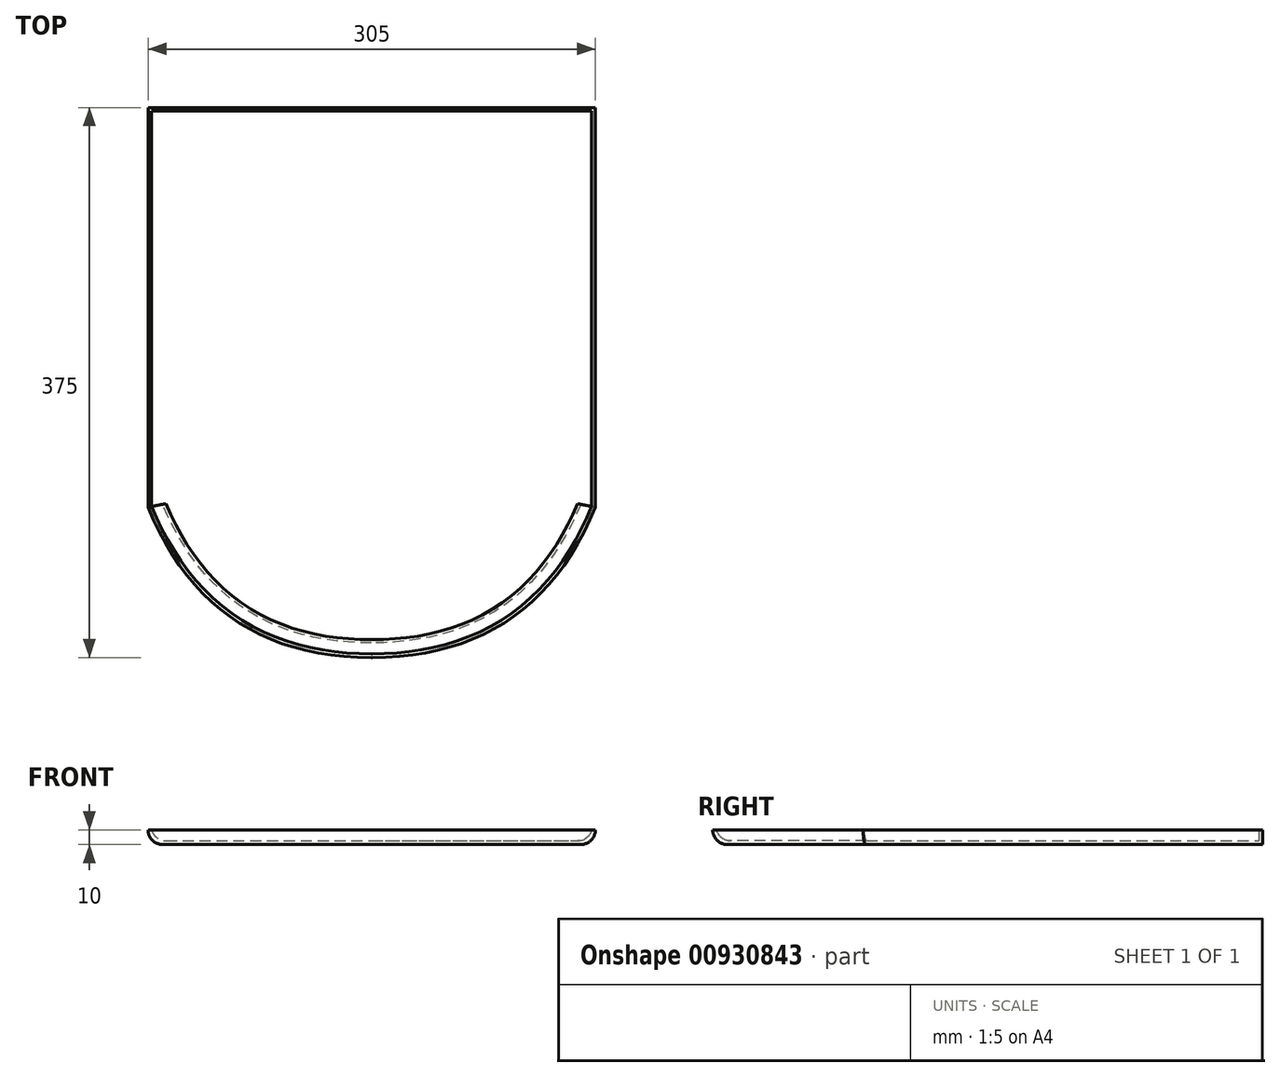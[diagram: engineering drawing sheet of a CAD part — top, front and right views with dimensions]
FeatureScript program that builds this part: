
annotation { "Feature Type Name" : "Feature", "Feature Type Description" : "" }
export const myFeature = defineFeature(function(context is Context, id is Id, definition is map)
    precondition{}
    {
        {
            var Q0;
            Q0=qCreatedBy(makeId("Top.planeOp"),FACE);
            var sketch = newSketch(context, id + "F0", { "sketchPlane" : qUnion([Q0])});
            skLineSegment(sketch, "E0.bottom", {"start": v(-152.5, 76.25) * mm, "end": v(152.5, 76.25) * mm});
            skLineSegment(sketch, "E0.top", {"start": v(-152.5, -76.25) * mm, "end": v(152.5, -76.25) * mm});
            skLineSegment(sketch, "E0.left", {"start": v(-152.5, 76.25) * mm, "end": v(-152.5, -76.25) * mm});
            skLineSegment(sketch, "E0.right", {"start": v(152.5, 76.25) * mm, "end": v(152.5, -76.25) * mm});
            skPoint(sketch, "E0.middle", {"position": v(0, 0) * mm});
            skLineSegment(sketch, "E1.bottom", {"start": v(-102.5, 76.25) * mm, "end": v(102.5, 76.25) * mm});
            skLineSegment(sketch, "E1.top", {"start": v(-102.5, 298.75) * mm, "end": v(102.5, 298.75) * mm});
            skLineSegment(sketch, "E1.left", {"start": v(-102.5, 76.25) * mm, "end": v(-102.5, 298.75) * mm});
            skLineSegment(sketch, "E1.right", {"start": v(102.5, 76.25) * mm, "end": v(102.5, 298.75) * mm});
            skPoint(sketch, "E2", {"position": v(0, 298.75) * mm});
            skSolve(sketch);
        }
        {
            var Q0;
            Q0=makeQuery(id+"F0.imprint","IMPRINT",FACE,{"disambiguationData":[TD([[makeQuery(id+"F0.imprint","IMPRINT",EDGE,{"derivedFrom":sQuery(id+"F0.wireOp",EDGE,"E1.bottom")}),1.0]])]});
            var Q1;
            Q1=makeQuery(id+"F0.imprint","IMPRINT",FACE,{"disambiguationData":[TD([[makeQuery(id+"F0.imprint","IMPRINT",EDGE,{"derivedFrom":sQuery(id+"F0.wireOp",EDGE,"E0.top")}),1.0]])]});
            extrude(context, id + "F1", {"entities" : qUnion([Q0, Q1]), "flatOperationType" : FlatOperationType.REMOVE, "depth" : 10 * mm, "offsetDistance" : 25 * mm, "domain" : OperationDomain.MODEL});
        }
        {
            var Q0;
            Q0=makeQuery(id+"F1.opExtrude","SWEPT_EDGE",EDGE,{"disambiguationData":[OSD([sQuery(id+"F0.wireOp",EDGE,"E0.bottom"),sQuery(id+"F0.wireOp",EDGE,"E0.left")])]});
            var Q1;
            Q1=makeQuery(id+"F1.opExtrude","SWEPT_EDGE",EDGE,{"disambiguationData":[OSD([sQuery(id+"F0.wireOp",EDGE,"E0.bottom"),sQuery(id+"F0.wireOp",EDGE,"E0.right")])]});
            chamfer(context, id + "F2", {"entities" : qUnion([Q0, Q1]), "width" : 50 * mm, "tangentPropagation" : true});
        }
        {
            var Q0;
            Q0=makeQuery(id+"F1.opExtrude","SWEPT_EDGE",EDGE,{"disambiguationData":[OSD([sQuery(id+"F0.wireOp",EDGE,"E0.top"),sQuery(id+"F0.wireOp",EDGE,"E0.left")])]});
            var Q1;
            Q1=makeQuery(id+"F1.opExtrude","SWEPT_EDGE",EDGE,{"disambiguationData":[OSD([sQuery(id+"F0.wireOp",EDGE,"E0.top"),sQuery(id+"F0.wireOp",EDGE,"E0.right")])]});
            fillet(context, id + "F3", {"entities" : qUnion([Q0, Q1]), "radius" : 165 * mm, "tangentPropagation" : true, "crossSection" : FilletCrossSection.CONIC, "rho" : 0.5, "defaultsChanged" : true, "vertexSettings" : [], "allowEdgeOverflow" : false});
        }
        {
            var Q0;
            Q0=qCreatedBy(makeId("Top.planeOp"),FACE);
            var sketch = newSketch(context, id + "F4", { "sketchPlane" : qUnion([Q0])});
            skLineSegment(sketch, "E3.bottom", {"start": v(-152.5, 298.75) * mm, "end": v(152.5, 298.75) * mm});
            skLineSegment(sketch, "E3.top", {"start": v(-152.5, 26.25) * mm, "end": v(152.5, 26.25) * mm});
            skLineSegment(sketch, "E3.left", {"start": v(-152.5, 298.75) * mm, "end": v(-152.5, 26.25) * mm});
            skLineSegment(sketch, "E3.right", {"start": v(152.5, 298.75) * mm, "end": v(152.5, 26.25) * mm});
            skSolve(sketch);
        }
        {
            var Q0;
            Q0=makeQuery(id+"F4.imprint","IMPRINT",FACE,{"disambiguationData":[TD([[makeQuery(id+"F4.imprint","IMPRINT",EDGE,{"derivedFrom":sQuery(id+"F4.wireOp",EDGE,"E3.bottom")}),-1.0]])]});
            extrude(context, id + "F5", {"entities" : qUnion([Q0]), "operationType" : NewBodyOperationType.ADD, "flatOperationType" : FlatOperationType.REMOVE, "depth" : 10 * mm, "offsetDistance" : 25 * mm, "domain" : OperationDomain.MODEL});
        }
        {
            var Q0;
            Q0=makeQuery(id+"F1.opExtrude","CAP_FACE",FACE,{"disambiguationData":[OSD([sQuery(id+"F0.wireOp",EDGE,"E0.bottom"),sQuery(id+"F0.wireOp",EDGE,"E0.top"),sQuery(id+"F0.wireOp",EDGE,"E0.left"),sQuery(id+"F0.wireOp",EDGE,"E0.right"),sQuery(id+"F0.wireOp",EDGE,"E1.top"),sQuery(id+"F0.wireOp",EDGE,"E1.left"),sQuery(id+"F0.wireOp",EDGE,"E1.right")])],"isStart":false});
            shell(context, id + "F6", {"entities" : qUnion([Q0]), "thickness" : 2.5 * mm});
        }
        {
            var Q0;
            {var subQ0=sQuery(id+"F4.wireOp",EDGE,"E3.bottom");var subQ1=sQuery(id+"F0.wireOp",EDGE,"E1.top");Q0=makeQuery(id+"F6.opShell","OFFSET_EDGE",EDGE,{"disambiguationData":[OSD([subQ1,subQ0]),TDD([makeQuery(id+"F5.boolean.opBoolean","MERGE",EDGE,{"derivedFrom":[makeQuery(id+"F1.opExtrude","CAP_EDGE",EDGE,{"disambiguationData":[OSD([subQ1])],"isStart":true}),makeQuery(id+"F5.opExtrude","CAP_EDGE",EDGE,{"disambiguationData":[OSD([subQ0])],"isStart":true})]})])]});}
            var Q1;
            {var subQ0=sQuery(id+"F4.wireOp",EDGE,"E3.left");Q1=makeQuery(id+"F6.opShell","OFFSET_EDGE",EDGE,{"disambiguationData":[OSD([subQ0]),TDD([makeQuery(id+"F5.opExtrude","CAP_EDGE",EDGE,{"disambiguationData":[OSD([subQ0])],"isStart":true})])]});}
            var Q2;
            {var subQ0=sQuery(id+"F4.wireOp",EDGE,"E3.right");Q2=makeQuery(id+"F6.opShell","OFFSET_EDGE",EDGE,{"disambiguationData":[OSD([subQ0]),TDD([makeQuery(id+"F5.opExtrude","CAP_EDGE",EDGE,{"disambiguationData":[OSD([subQ0])],"isStart":true})])]});}
            var Q3;
            {var subQ0=sQuery(id+"F0.wireOp",EDGE,"E1.right");var subQ1=sQuery(id+"F0.wireOp",EDGE,"E1.left");var subQ2=sQuery(id+"F0.wireOp",EDGE,"E1.top");var subQ3=sQuery(id+"F0.wireOp",EDGE,"E0.right");var subQ4=sQuery(id+"F0.wireOp",EDGE,"E0.left");var subQ5=sQuery(id+"F0.wireOp",EDGE,"E0.top");var subQ6=sQuery(id+"F0.wireOp",EDGE,"E0.bottom");Q3=makeQuery(id+"F6.opShell","OFFSET_EDGE",EDGE,{"disambiguationData":[OSD([subQ6,subQ5,subQ4,subQ3,subQ2,subQ1,subQ0]),TDD([makeQuery(id+"F3.opFillet","BLEND_EDGE",EDGE,{"disambiguationData":[OD(1.0)],"blendedFrom":[makeQuery(id+"F1.opExtrude","SWEPT_EDGE",EDGE,{"disambiguationData":[OSD([subQ5,subQ3])]}),makeQuery(id+"F1.opExtrude","CAP_FACE",FACE,{"disambiguationData":[OSD([subQ6,subQ5,subQ4,subQ3,subQ2,subQ1,subQ0])],"isStart":true})],"blendedInto":[makeQuery(id+"F1.opExtrude","CAP_FACE",FACE,{"disambiguationData":[OSD([subQ6,subQ5,subQ4,subQ3,subQ2,subQ1,subQ0])],"isStart":true})]})])]});}
            var Q4;
            {var subQ0=sQuery(id+"F0.wireOp",EDGE,"E1.right");var subQ1=sQuery(id+"F0.wireOp",EDGE,"E1.left");var subQ2=sQuery(id+"F0.wireOp",EDGE,"E1.top");var subQ3=sQuery(id+"F0.wireOp",EDGE,"E0.right");var subQ4=sQuery(id+"F0.wireOp",EDGE,"E0.left");var subQ5=sQuery(id+"F0.wireOp",EDGE,"E0.top");var subQ6=sQuery(id+"F0.wireOp",EDGE,"E0.bottom");Q4=makeQuery(id+"F6.opShell","OFFSET_EDGE",EDGE,{"disambiguationData":[OSD([subQ6,subQ5,subQ4,subQ3,subQ2,subQ1,subQ0]),TDD([makeQuery(id+"F3.opFillet","BLEND_EDGE",EDGE,{"blendedFrom":[makeQuery(id+"F1.opExtrude","SWEPT_EDGE",EDGE,{"disambiguationData":[OSD([subQ5,subQ4])]}),makeQuery(id+"F1.opExtrude","CAP_FACE",FACE,{"disambiguationData":[OSD([subQ6,subQ5,subQ4,subQ3,subQ2,subQ1,subQ0])],"isStart":true})],"blendedInto":[makeQuery(id+"F1.opExtrude","CAP_FACE",FACE,{"disambiguationData":[OSD([subQ6,subQ5,subQ4,subQ3,subQ2,subQ1,subQ0])],"isStart":true})]})])]});}
            var Q5;
            {var subQ0=sQuery(id+"F0.wireOp",EDGE,"E0.left");var subQ1=sQuery(id+"F0.wireOp",EDGE,"E0.top");Q5=makeQuery(id+"F3.opFillet","BLEND_EDGE",EDGE,{"blendedFrom":[makeQuery(id+"F1.opExtrude","SWEPT_EDGE",EDGE,{"disambiguationData":[OSD([subQ1,subQ0])]}),makeQuery(id+"F1.opExtrude","CAP_FACE",FACE,{"disambiguationData":[OSD([sQuery(id+"F0.wireOp",EDGE,"E0.bottom"),subQ1,subQ0,sQuery(id+"F0.wireOp",EDGE,"E0.right"),sQuery(id+"F0.wireOp",EDGE,"E1.top"),sQuery(id+"F0.wireOp",EDGE,"E1.left"),sQuery(id+"F0.wireOp",EDGE,"E1.right")])],"isStart":true})],"blendedInto":[makeQuery(id+"F1.opExtrude","CAP_FACE",FACE,{"disambiguationData":[OSD([sQuery(id+"F0.wireOp",EDGE,"E0.bottom"),subQ1,subQ0,sQuery(id+"F0.wireOp",EDGE,"E0.right"),sQuery(id+"F0.wireOp",EDGE,"E1.top"),sQuery(id+"F0.wireOp",EDGE,"E1.left"),sQuery(id+"F0.wireOp",EDGE,"E1.right")])],"isStart":true})]});}
            var Q6;
            {var subQ0=sQuery(id+"F0.wireOp",EDGE,"E0.right");var subQ1=sQuery(id+"F0.wireOp",EDGE,"E0.top");Q6=makeQuery(id+"F3.opFillet","BLEND_EDGE",EDGE,{"disambiguationData":[OD(1.0)],"blendedFrom":[makeQuery(id+"F1.opExtrude","SWEPT_EDGE",EDGE,{"disambiguationData":[OSD([subQ1,subQ0])]}),makeQuery(id+"F1.opExtrude","CAP_FACE",FACE,{"disambiguationData":[OSD([sQuery(id+"F0.wireOp",EDGE,"E0.bottom"),subQ1,sQuery(id+"F0.wireOp",EDGE,"E0.left"),subQ0,sQuery(id+"F0.wireOp",EDGE,"E1.top"),sQuery(id+"F0.wireOp",EDGE,"E1.left"),sQuery(id+"F0.wireOp",EDGE,"E1.right")])],"isStart":true})],"blendedInto":[makeQuery(id+"F1.opExtrude","CAP_FACE",FACE,{"disambiguationData":[OSD([sQuery(id+"F0.wireOp",EDGE,"E0.bottom"),subQ1,sQuery(id+"F0.wireOp",EDGE,"E0.left"),subQ0,sQuery(id+"F0.wireOp",EDGE,"E1.top"),sQuery(id+"F0.wireOp",EDGE,"E1.left"),sQuery(id+"F0.wireOp",EDGE,"E1.right")])],"isStart":true})]});}
            var Q7;
            Q7=makeQuery(id+"F5.opExtrude","CAP_EDGE",EDGE,{"disambiguationData":[OSD([sQuery(id+"F4.wireOp",EDGE,"E3.right")])],"isStart":true});
            var Q8;
            Q8=makeQuery(id+"F5.boolean.opBoolean","MERGE",EDGE,{"derivedFrom":[makeQuery(id+"F1.opExtrude","CAP_EDGE",EDGE,{"disambiguationData":[OSD([sQuery(id+"F0.wireOp",EDGE,"E1.top")])],"isStart":true}),makeQuery(id+"F5.opExtrude","CAP_EDGE",EDGE,{"disambiguationData":[OSD([sQuery(id+"F4.wireOp",EDGE,"E3.bottom")])],"isStart":true})]});
            var Q9;
            Q9=makeQuery(id+"F5.opExtrude","CAP_EDGE",EDGE,{"disambiguationData":[OSD([sQuery(id+"F4.wireOp",EDGE,"E3.left")])],"isStart":true});
            fillet(context, id + "F7", {"entities" : qUnion([Q0, Q1, Q2, Q3, Q4, Q5, Q6, Q7, Q8, Q9]), "tangentPropagation" : true, "radius" : 10 * mm, "defaultsChanged" : false, "vertexSettings" : [], "allowEdgeOverflow" : false});
        }
    });
